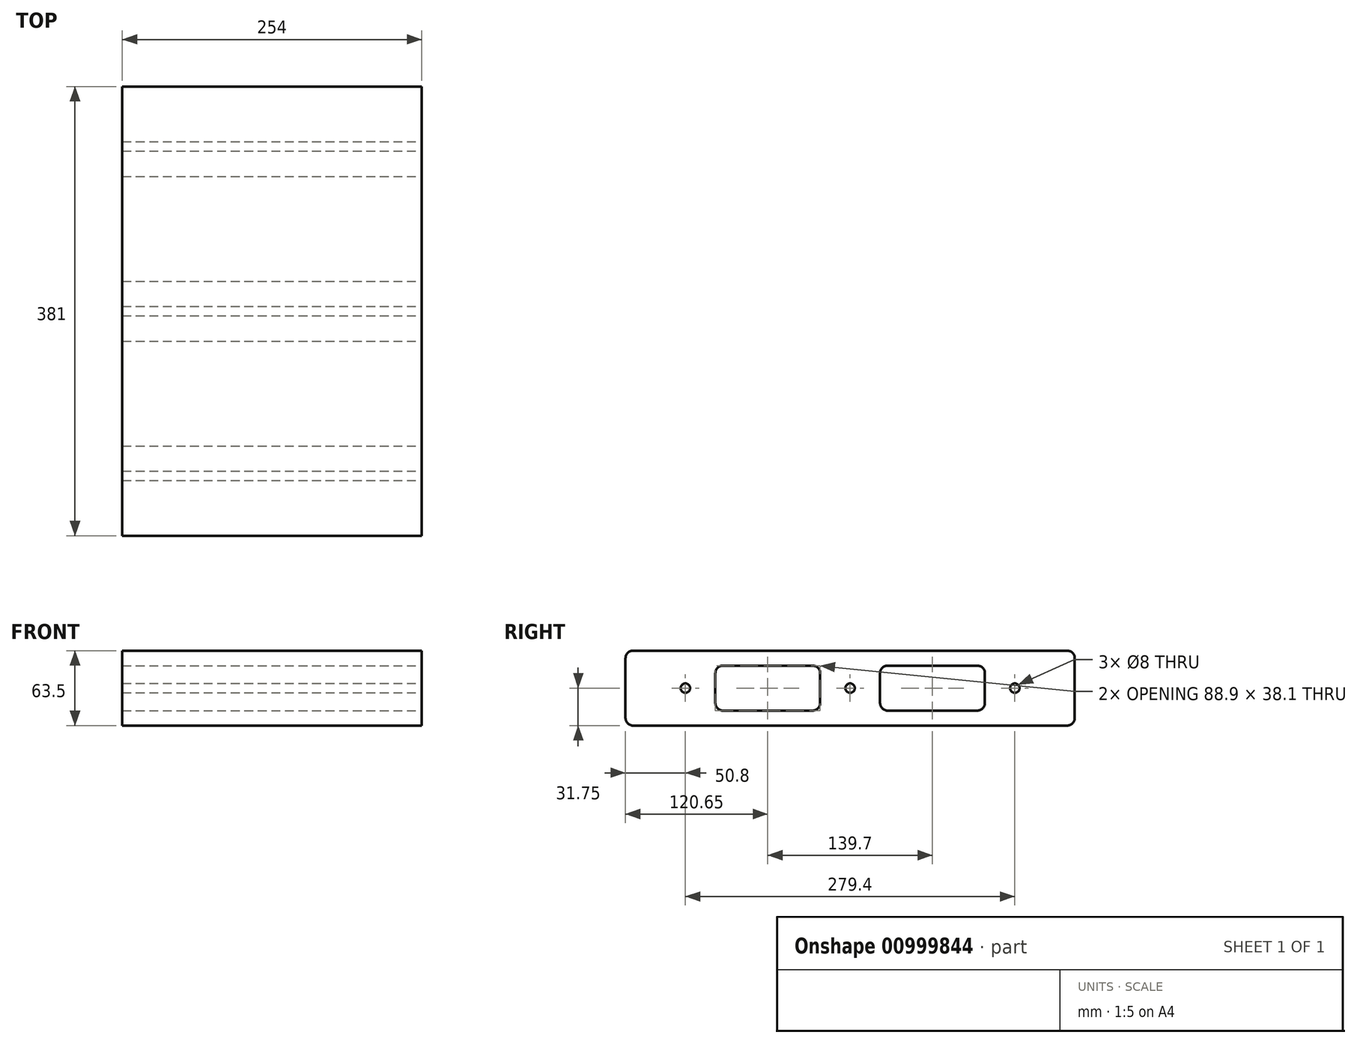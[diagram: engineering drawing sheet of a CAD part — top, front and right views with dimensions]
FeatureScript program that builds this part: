
annotation { "Feature Type Name" : "Feature", "Feature Type Description" : "" }
export const myFeature = defineFeature(function(context is Context, id is Id, definition is map)
    precondition{}
    {
        {
            var Q0;
            Q0=qCreatedBy(makeId("Right.planeOp"),FACE);
            var sketch = newSketch(context, id + "F0", { "sketchPlane" : qUnion([Q0])});
            skLineSegment(sketch, "E0.bottom", {"start": v(190.5, 31.75) * mm, "end": v(-190.5, 31.75) * mm});
            skLineSegment(sketch, "E0.top", {"start": v(190.5, -31.75) * mm, "end": v(-190.5, -31.75) * mm});
            skLineSegment(sketch, "E0.left", {"start": v(190.5, 31.75) * mm, "end": v(190.5, -31.75) * mm});
            skLineSegment(sketch, "E0.right", {"start": v(-190.5, 31.75) * mm, "end": v(-190.5, -31.75) * mm});
            skPoint(sketch, "E0.middle", {"position": v(0, 0) * mm});
            skPoint(sketch, "E1.visualSharp", {"position": v(-190.5, 31.75) * mm});
            skLineSegment(sketch, "E1.filletArc", {"start": v(-190.5, 31.75) * mm, "end": v(-190.5, 31.75) * mm});
            skPoint(sketch, "E2.visualSharp", {"position": v(190.5, 31.75) * mm});
            skLineSegment(sketch, "E2.filletArc", {"start": v(190.5, 31.75) * mm, "end": v(190.5, 31.75) * mm});
            skPoint(sketch, "E3.visualSharp", {"position": v(190.5, -31.75) * mm});
            skLineSegment(sketch, "E3.filletArc", {"start": v(190.5, -31.75) * mm, "end": v(190.5, -31.75) * mm});
            skPoint(sketch, "E4.visualSharp", {"position": v(-190.5, -31.75) * mm});
            skLineSegment(sketch, "E4.filletArc", {"start": v(-190.5, -31.75) * mm, "end": v(-190.5, -31.75) * mm});
            skCircle(sketch, "E5", {"center": v(0, 0) * mm, "radius": 4 * mm});
            skCircle(sketch, "E6", {"center": v(-139.7, 0) * mm, "radius": 4 * mm});
            skCircle(sketch, "E7", {"center": v(139.7, 0) * mm, "radius": 4 * mm});
            skLineSegment(sketch, "E8", {"start": v(0, 0) * mm, "end": v(-69.85, 0) * mm});
            skLineSegment(sketch, "E9", {"start": v(0, 0) * mm, "end": v(69.85, 0) * mm});
            skLineSegment(sketch, "E10.bottom", {"start": v(-31.75, -19.05) * mm, "end": v(-107.95, -19.05) * mm});
            skLineSegment(sketch, "E10.top", {"start": v(-31.75, 19.05) * mm, "end": v(-107.95, 19.05) * mm});
            skLineSegment(sketch, "E10.left", {"start": v(-25.4, -12.7) * mm, "end": v(-25.4, 12.7) * mm});
            skLineSegment(sketch, "E10.right", {"start": v(-114.3, -12.7) * mm, "end": v(-114.3, 12.7) * mm});
            skPoint(sketch, "E10.middle", {"position": v(-69.85, 0) * mm});
            skLineSegment(sketch, "E11.bottom", {"start": v(107.95, -19.05) * mm, "end": v(31.75, -19.05) * mm});
            skLineSegment(sketch, "E11.top", {"start": v(107.95, 19.05) * mm, "end": v(31.75, 19.05) * mm});
            skLineSegment(sketch, "E11.left", {"start": v(114.3, -12.7) * mm, "end": v(114.3, 12.7) * mm});
            skLineSegment(sketch, "E11.right", {"start": v(25.4, -12.7) * mm, "end": v(25.4, 12.7) * mm});
            skPoint(sketch, "E11.middle", {"position": v(69.85, 0) * mm});
            skPoint(sketch, "E12.visualSharp", {"position": v(-114.3, 19.05) * mm});
            skArc(sketch, "E12.filletArc", {"start": v(-107.95, 19.05) * mm, "mid": v(-112.44, 17.2) * mm, "end": v(-114.3, 12.7) * mm});
            skPoint(sketch, "E13.visualSharp", {"position": v(-114.3, -19.05) * mm});
            skArc(sketch, "E13.filletArc", {"start": v(-114.3, -12.7) * mm, "mid": v(-112.44, -17.2) * mm, "end": v(-107.95, -19.05) * mm});
            skPoint(sketch, "E14.visualSharp", {"position": v(114.3, 19.05) * mm});
            skArc(sketch, "E14.filletArc", {"start": v(114.3, 12.7) * mm, "mid": v(112.44, 17.2) * mm, "end": v(107.95, 19.05) * mm});
            skPoint(sketch, "E15.visualSharp", {"position": v(114.3, -19.05) * mm});
            skArc(sketch, "E15.filletArc", {"start": v(107.95, -19.05) * mm, "mid": v(112.44, -17.2) * mm, "end": v(114.3, -12.7) * mm});
            skPoint(sketch, "E16.visualSharp", {"position": v(-25.4, -19.05) * mm});
            skArc(sketch, "E16.filletArc", {"start": v(-31.75, -19.05) * mm, "mid": v(-27.26, -17.2) * mm, "end": v(-25.4, -12.7) * mm});
            skPoint(sketch, "E17.visualSharp", {"position": v(-25.4, 19.05) * mm});
            skArc(sketch, "E17.filletArc", {"start": v(-25.4, 12.7) * mm, "mid": v(-27.26, 17.2) * mm, "end": v(-31.75, 19.05) * mm});
            skPoint(sketch, "E18.visualSharp", {"position": v(25.4, -19.05) * mm});
            skArc(sketch, "E18.filletArc", {"start": v(25.4, -12.7) * mm, "mid": v(27.26, -17.2) * mm, "end": v(31.75, -19.05) * mm});
            skPoint(sketch, "E19.visualSharp", {"position": v(25.4, 19.05) * mm});
            skArc(sketch, "E19.filletArc", {"start": v(31.75, 19.05) * mm, "mid": v(27.26, 17.2) * mm, "end": v(25.4, 12.7) * mm});
            skSolve(sketch);
        }
        {
            var Q0;
            Q0=makeQuery(id+"F0.imprint","IMPRINT",FACE,{"disambiguationData":[TD([[makeQuery(id+"F0.imprint","IMPRINT",EDGE,{"derivedFrom":sQuery(id+"F0.wireOp",EDGE,"E0.bottom")}),1.0]])]});
            extrude(context, id + "F1", {"entities" : qUnion([Q0]), "oppositeDirection" : true, "depth" : 254 * mm, "offsetDistance" : 25.4 * mm});
        }
        {
            var Q0;
            Q0=makeQuery(id+"F1.opExtrude","SWEPT_EDGE",EDGE,{"disambiguationData":[OSD([sQuery(id+"F0.wireOp",EDGE,"E0.top"),sQuery(id+"F0.wireOp",EDGE,"E0.right")])]});
            var Q1;
            Q1=makeQuery(id+"F1.opExtrude","SWEPT_EDGE",EDGE,{"disambiguationData":[OSD([sQuery(id+"F0.wireOp",EDGE,"E0.bottom"),sQuery(id+"F0.wireOp",EDGE,"E0.right")])]});
            var Q2;
            Q2=makeQuery(id+"F1.opExtrude","SWEPT_EDGE",EDGE,{"disambiguationData":[OSD([sQuery(id+"F0.wireOp",EDGE,"E0.bottom"),sQuery(id+"F0.wireOp",EDGE,"E0.left")])]});
            var Q3;
            Q3=makeQuery(id+"F1.opExtrude","SWEPT_EDGE",EDGE,{"disambiguationData":[OSD([sQuery(id+"F0.wireOp",EDGE,"E0.top"),sQuery(id+"F0.wireOp",EDGE,"E0.left")])]});
            fillet(context, id + "F2", {"entities" : qUnion([Q0, Q1, Q2, Q3]), "radius" : 6.35 * mm, "tangentPropagation" : true, "allowEdgeOverflow" : false});
        }
    });
